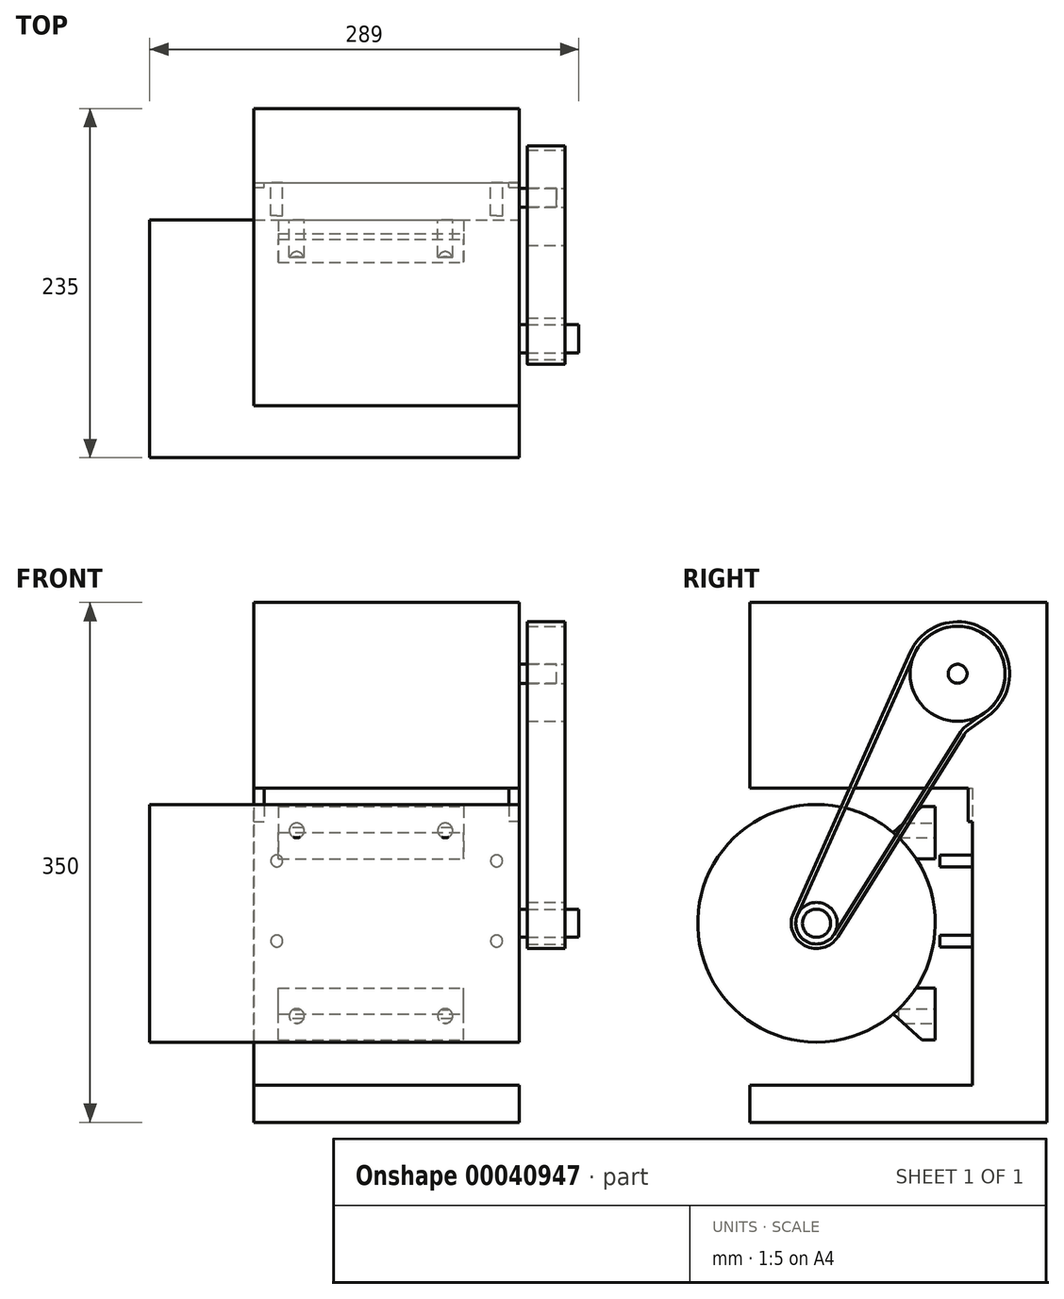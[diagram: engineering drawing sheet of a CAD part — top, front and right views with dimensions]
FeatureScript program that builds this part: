
annotation { "Feature Type Name" : "Feature", "Feature Type Description" : "" }
export const myFeature = defineFeature(function(context is Context, id is Id, definition is map)
    precondition{}
    {
        {
            var Q0;
            Q0=qCreatedBy(makeId("Right.planeOp"),FACE);
            var sketch = newSketch(context, id + "F0", { "sketchPlane" : qUnion([Q0])});
            skCircle(sketch, "E0", {"center": v(-10, 126) * mm, "radius": 6.38 * mm});
            skSolve(sketch);
        }
        {
            var Q0;
            Q0=makeQuery(id+"F0.imprint","IMPRINT",FACE,{"disambiguationData":[TD([[makeQuery(id+"F0.imprint","IMPRINT",EDGE,{"derivedFrom":sQuery(id+"F0.wireOp",EDGE,"E0")}),1.0]])]});
            extrude(context, id + "F1", {"entities" : qUnion([Q0]), "depth" : 25 * mm});
        }
        {
            var Q0;
            Q0=qCreatedBy(makeId("Right.planeOp"),FACE);
            var sketch = newSketch(context, id + "F2", { "sketchPlane" : qUnion([Q0])});
            skLineSegment(sketch, "E1", {"start": v(0, -151) * mm, "end": v(0, 49) * mm});
            skLineSegment(sketch, "E2", {"start": v(0, 49) * mm, "end": v(-150, 49) * mm});
            skLineSegment(sketch, "E3", {"start": v(-150, 49) * mm, "end": v(-150, 174) * mm});
            skLineSegment(sketch, "E4", {"start": v(-150, 174) * mm, "end": v(50, 174) * mm});
            skLineSegment(sketch, "E5", {"start": v(50, 174) * mm, "end": v(50, -176) * mm});
            skLineSegment(sketch, "E6", {"start": v(50, -176) * mm, "end": v(-150, -176) * mm});
            skLineSegment(sketch, "E7", {"start": v(-150, -176) * mm, "end": v(-150, -151) * mm});
            skLineSegment(sketch, "E8", {"start": v(-150, -151) * mm, "end": v(0, -151) * mm});
            skSolve(sketch);
        }
        {
            var Q0;
            Q0=makeQuery(id+"F2.imprint","IMPRINT",FACE,{"disambiguationData":[TD([[makeQuery(id+"F2.imprint","IMPRINT",EDGE,{"derivedFrom":sQuery(id+"F2.wireOp",EDGE,"E1")}),-1.0]])]});
            extrude(context, id + "F3", {"entities" : qUnion([Q0]), "operationType" : NewBodyOperationType.ADD, "oppositeDirection" : true, "depth" : (148 + 15.4 + 15.4) * mm});
        }
        {
            var Q0;
            Q0=qCreatedBy(makeId("Front.planeOp"),FACE);
            var sketch = newSketch(context, id + "F4", { "sketchPlane" : qUnion([Q0])});
            skCircle(sketch, "E9", {"center": v(-15.4, 0) * mm, "radius": 4 * mm});
            skCircle(sketch, "E10.0.1.0", {"center": v(-15.4, -54) * mm, "radius": 4 * mm});
            skCircle(sketch, "E10.1.0.0", {"center": v(-163.4, 0) * mm, "radius": 4 * mm});
            skCircle(sketch, "E10.1.1.0", {"center": v(-163.4, -54) * mm, "radius": 4 * mm});
            skLineSegment(sketch, "E10.direction1", {"start": v(-15.4, 0) * mm, "end": v(-163.4, 0) * mm, "construction": true});
            skLineSegment(sketch, "E10.direction2", {"start": v(-15.4, 0) * mm, "end": v(-15.4, -54) * mm, "construction": true});
            skSolve(sketch);
        }
        {
            var Q0;
            Q0=makeQuery(id+"F4.imprint","IMPRINT",FACE,{"disambiguationData":[TD([[makeQuery(id+"F4.imprint","IMPRINT",EDGE,{"derivedFrom":sQuery(id+"F4.wireOp",EDGE,"E9")}),1.0]])]});
            var Q1;
            Q1=makeQuery(id+"F4.imprint","IMPRINT",FACE,{"disambiguationData":[TD([[makeQuery(id+"F4.imprint","IMPRINT",EDGE,{"derivedFrom":sQuery(id+"F4.wireOp",EDGE,"E10.1.0.0")}),1.0]])]});
            var Q2;
            Q2=makeQuery(id+"F4.imprint","IMPRINT",FACE,{"disambiguationData":[TD([[makeQuery(id+"F4.imprint","IMPRINT",EDGE,{"derivedFrom":sQuery(id+"F4.wireOp",EDGE,"E10.1.1.0")}),1.0]])]});
            var Q3;
            Q3=makeQuery(id+"F4.imprint","IMPRINT",FACE,{"disambiguationData":[TD([[makeQuery(id+"F4.imprint","IMPRINT",EDGE,{"derivedFrom":sQuery(id+"F4.wireOp",EDGE,"E10.0.1.0")}),1.0]])]});
            extrude(context, id + "F5", {"entities" : qUnion([Q0, Q1, Q2, Q3]), "operationType" : NewBodyOperationType.ADD, "depth" : 22 * mm});
        }
        {
            var Q0;
            Q0=makeQuery(id+"F3.opExtrude","SWEPT_FACE",FACE,{"disambiguationData":[OSD([sQuery(id+"F2.wireOp",EDGE,"E1")])]});
            var sketch = newSketch(context, id + "F6", { "sketchPlane" : qUnion([Q0])});
            skLineSegment(sketch, "E11.bottom", {"start": v(0, 49) * mm, "end": v(-7, 49) * mm});
            skLineSegment(sketch, "E11.top", {"start": v(0, 26.4) * mm, "end": v(-7, 26.4) * mm});
            skLineSegment(sketch, "E11.left", {"start": v(0, 49) * mm, "end": v(0, 26.4) * mm});
            skLineSegment(sketch, "E11.right", {"start": v(-7, 49) * mm, "end": v(-7, 26.4) * mm});
            skLineSegment(sketch, "E12.bottom", {"start": v(-178.8, 49) * mm, "end": v(-171.8, 49) * mm});
            skLineSegment(sketch, "E12.top", {"start": v(-178.8, 26.4) * mm, "end": v(-171.8, 26.4) * mm});
            skLineSegment(sketch, "E12.left", {"start": v(-178.8, 49) * mm, "end": v(-178.8, 26.4) * mm});
            skLineSegment(sketch, "E12.right", {"start": v(-171.8, 49) * mm, "end": v(-171.8, 26.4) * mm});
            skSolve(sketch);
        }
        {
            var Q0;
            Q0=makeQuery(id+"F6.imprint","IMPRINT",FACE,{"disambiguationData":[TD([[makeQuery(id+"F6.imprint","IMPRINT",EDGE,{"derivedFrom":sQuery(id+"F6.wireOp",EDGE,"E11.bottom")}),-1.0]])]});
            var Q1;
            Q1=makeQuery(id+"F6.imprint","IMPRINT",FACE,{"disambiguationData":[TD([[makeQuery(id+"F6.imprint","IMPRINT",EDGE,{"derivedFrom":sQuery(id+"F6.wireOp",EDGE,"E12.bottom")}),-1.0]])]});
            extrude(context, id + "F7", {"entities" : qUnion([Q0, Q1]), "operationType" : NewBodyOperationType.ADD, "depth" : 3 * mm});
        }
        {
            var Q0;
            Q0=qCreatedBy(makeId("Right.planeOp"),FACE);
            var sketch = newSketch(context, id + "F8", { "sketchPlane" : qUnion([Q0])});
            skCircle(sketch, "E13", {"center": v(-105, -42) * mm, "radius": 80 * mm});
            skSolve(sketch);
        }
        {
            var Q0;
            Q0=makeQuery(id+"F8.imprint","IMPRINT",FACE,{"disambiguationData":[TD([[makeQuery(id+"F8.imprint","IMPRINT",EDGE,{"derivedFrom":sQuery(id+"F8.wireOp",EDGE,"E13")}),1.0]])]});
            extrude(context, id + "F9", {"entities" : qUnion([Q0]), "oppositeDirection" : true, "depth" : 249 * mm});
        }
        {
            var Q0;
            Q0=qCreatedBy(makeId("Right.planeOp"),FACE);
            cPlane(context, id + "F10", {"entities" : qUnion([Q0]), "cplaneType" : CPlaneType.OFFSET, "offset" : 37.5 * mm, "oppositeDirection" : true, "width" : 150 * mm, "height" : 150 * mm});
        }
        {
            var Q0;
            Q0=qCreatedBy(id+"F10.planeOp",FACE);
            var sketch = newSketch(context, id + "F11", { "sketchPlane" : qUnion([Q0])});
            skLineSegment(sketch, "E14", {"start": v(-25, 36.5) * mm, "end": v(-25, 1.5) * mm});
            skLineSegment(sketch, "E15", {"start": v(-25, 1.5) * mm, "end": v(-37.86, 1.5) * mm});
            skLineSegment(sketch, "E16", {"start": v(-25, 36.5) * mm, "end": v(-34, 36.5) * mm});
            skLineSegment(sketch, "E17", {"start": v(-34, 36.5) * mm, "end": v(-53.41, 19.15) * mm});
            skArc(sketch, "E18", {"start": v(-37.86, 1.5) * mm, "mid": v(-44.99, 10.9) * mm, "end": v(-53.41, 19.15) * mm});
            skLineSegment(sketch, "E19", {"start": v(-105, -42) * mm, "end": v(-57.73, -42) * mm});
            skLineSegment(sketch, "E20.MirrorCS", {"start": v(-25, -85.5) * mm, "end": v(-37.86, -85.5) * mm});
            skLineSegment(sketch, "E21.MirrorCS", {"start": v(-25, -120.5) * mm, "end": v(-25, -85.5) * mm});
            skLineSegment(sketch, "E22.MirrorCS", {"start": v(-34, -120.5) * mm, "end": v(-53.41, -103.15) * mm});
            skLineSegment(sketch, "E23.MirrorCS", {"start": v(-25, -120.5) * mm, "end": v(-34, -120.5) * mm});
            skArc(sketch, "E24.MirrorCS", {"start": v(-37.86, -85.5) * mm, "mid": v(-44.99, -94.9) * mm, "end": v(-53.41, -103.15) * mm});
            skSolve(sketch);
        }
        {
            var Q0;
            Q0=makeQuery(id+"F11.imprint","IMPRINT",FACE,{"disambiguationData":[TD([[makeQuery(id+"F11.imprint","IMPRINT",EDGE,{"derivedFrom":sQuery(id+"F11.wireOp",EDGE,"E14")}),-1.0]])]});
            var Q1;
            Q1=makeQuery(id+"F11.imprint","IMPRINT",FACE,{"disambiguationData":[TD([[makeQuery(id+"F11.imprint","IMPRINT",EDGE,{"derivedFrom":sQuery(id+"F11.wireOp",EDGE,"E20.MirrorCS")}),1.0]])]});
            extrude(context, id + "F12", {"entities" : qUnion([Q0, Q1]), "oppositeDirection" : true, "depth" : 125 * mm});
        }
        {
            var Q0;
            Q0=qCreatedBy(makeId("Right.planeOp"),FACE);
            cPlane(context, id + "F13", {"entities" : qUnion([Q0]), "cplaneType" : CPlaneType.OFFSET, "offset" : (46 - 15.4) * mm, "width" : 150 * mm, "height" : 150 * mm});
        }
        {
            var Q0;
            Q0=qCreatedBy(id+"F13.planeOp",FACE);
            var sketch = newSketch(context, id + "F14", { "sketchPlane" : qUnion([Q0])});
            skCircle(sketch, "E25", {"center": v(-10, 126) * mm, "radius": 32 * mm});
            skCircle(sketch, "E26", {"center": v(-10, 126) * mm, "radius": 6.38 * mm});
            skSolve(sketch);
        }
        {
            var Q0;
            Q0=makeQuery(id+"F14.imprint","IMPRINT",FACE,{"disambiguationData":[TD([[makeQuery(id+"F14.imprint","IMPRINT",EDGE,{"derivedFrom":sQuery(id+"F14.wireOp",EDGE,"E25")}),1.0]])]});
            extrude(context, id + "F15", {"entities" : qUnion([Q0]), "oppositeDirection" : true, "depth" : 25.4 * mm});
        }
        {
            var Q0;
            Q0=qCreatedBy(id+"F13.planeOp",FACE);
            var sketch = newSketch(context, id + "F16", { "sketchPlane" : qUnion([Q0])});
            skCircle(sketch, "E27", {"center": v(-105, -42) * mm, "radius": 14 * mm});
            skCircle(sketch, "E28", {"center": v(-105, -42) * mm, "radius": 9.5 * mm});
            skSolve(sketch);
        }
        {
            var Q0;
            Q0=makeQuery(id+"F16.imprint","IMPRINT",FACE,{"disambiguationData":[TD([[makeQuery(id+"F16.imprint","IMPRINT",EDGE,{"derivedFrom":sQuery(id+"F16.wireOp",EDGE,"E27")}),1.0]])]});
            extrude(context, id + "F17", {"entities" : qUnion([Q0]), "oppositeDirection" : true, "depth" : 25.4 * mm});
        }
        {
            var Q0;
            Q0=makeQuery(id+"F12.opExtrude","SWEPT_FACE",FACE,{"disambiguationData":[OSD([sQuery(id+"F11.wireOp",EDGE,"E21.MirrorCS")])]});
            var sketch = newSketch(context, id + "F18", { "sketchPlane" : qUnion([Q0])});
            skCircle(sketch, "E29", {"center": v(50, 20.5) * mm, "radius": 5 * mm});
            skCircle(sketch, "E30.0.1.0", {"center": v(50, -104.5) * mm, "radius": 5 * mm});
            skCircle(sketch, "E30.1.0.0", {"center": v(150, 20.5) * mm, "radius": 5 * mm});
            skCircle(sketch, "E30.1.1.0", {"center": v(150, -104.5) * mm, "radius": 5 * mm});
            skLineSegment(sketch, "E30.direction1", {"start": v(50, 20.5) * mm, "end": v(150, 20.5) * mm, "construction": true});
            skLineSegment(sketch, "E30.direction2", {"start": v(50, 20.5) * mm, "end": v(50, -104.5) * mm, "construction": true});
            skSolve(sketch);
        }
        {
            var Q0;
            Q0=makeQuery(id+"F18.imprint","IMPRINT",FACE,{"disambiguationData":[TD([[makeQuery(id+"F18.imprint","IMPRINT",EDGE,{"derivedFrom":sQuery(id+"F18.wireOp",EDGE,"E29")}),1.0]])]});
            var Q1;
            Q1=makeQuery(id+"F18.imprint","IMPRINT",FACE,{"disambiguationData":[TD([[makeQuery(id+"F18.imprint","IMPRINT",EDGE,{"derivedFrom":sQuery(id+"F18.wireOp",EDGE,"E30.1.0.0")}),1.0]])]});
            var Q2;
            Q2=makeQuery(id+"F18.imprint","IMPRINT",FACE,{"disambiguationData":[TD([[makeQuery(id+"F18.imprint","IMPRINT",EDGE,{"derivedFrom":sQuery(id+"F18.wireOp",EDGE,"E30.1.1.0")}),1.0]])]});
            var Q3;
            Q3=makeQuery(id+"F18.imprint","IMPRINT",FACE,{"disambiguationData":[TD([[makeQuery(id+"F18.imprint","IMPRINT",EDGE,{"derivedFrom":sQuery(id+"F18.wireOp",EDGE,"E30.0.1.0")}),1.0]])]});
            extrude(context, id + "F19", {"entities" : qUnion([Q0, Q1, Q2, Q3]), "operationType" : NewBodyOperationType.REMOVE, "oppositeDirection" : true, "depth" : 25 * mm});
        }
        {
            var Q0;
            Q0=makeQuery(id+"F9.opExtrude","CAP_FACE",FACE,{"disambiguationData":[OSD([sQuery(id+"F8.wireOp",EDGE,"E13")])],"isStart":true});
            var sketch = newSketch(context, id + "F20", { "sketchPlane" : qUnion([Q0])});
            skCircle(sketch, "E31", {"center": v(-105, -42) * mm, "radius": 9.5 * mm});
            skSolve(sketch);
        }
        {
            var Q0;
            Q0=makeQuery(id+"F20.imprint","IMPRINT",FACE,{"disambiguationData":[TD([[makeQuery(id+"F20.imprint","IMPRINT",EDGE,{"derivedFrom":sQuery(id+"F20.wireOp",EDGE,"E31")}),1.0]])]});
            extrude(context, id + "F21", {"entities" : qUnion([Q0]), "depth" : 40 * mm});
        }
        {
            var Q0;
            Q0=qCreatedBy(id+"F13.planeOp",FACE);
            var sketch = newSketch(context, id + "F22", { "sketchPlane" : qUnion([Q0])});
            skArc(sketch, "E32.0", {"start": v(8.64, 100) * mm, "mid": v(10.25, 150.78) * mm, "end": v(-39.2, 139.08) * mm});
            skArc(sketch, "E33.0", {"start": v(-117.78, -36.28) * mm, "mid": v(-111.59, -54.35) * mm, "end": v(-93.13, -49.42) * mm});
            skLineSegment(sketch, "E34", {"start": v(-117.78, -36.28) * mm, "end": v(-39.2, 139.08) * mm});
            skLineSegment(sketch, "E35", {"start": v(8.64, 100) * mm, "end": v(-4.5, 90.57) * mm});
            skLineSegment(sketch, "E36", {"start": v(-93.13, -49.42) * mm, "end": v(-7.96, 86.89) * mm});
            skArc(sketch, "E37", {"start": v(-4.5, 90.57) * mm, "mid": v(-6.41, 88.9) * mm, "end": v(-7.96, 86.89) * mm});
            skArc(sketch, "E38.0", {"start": v(-120.51, -35.05) * mm, "mid": v(-113, -57) * mm, "end": v(-90.58, -51) * mm});
            skArc(sketch, "E38.1", {"start": v(10.4, 97.55) * mm, "mid": v(12.15, 153.1) * mm, "end": v(-41.94, 140.31) * mm});
            skLineSegment(sketch, "E38.2", {"start": v(10.4, 97.55) * mm, "end": v(-2.76, 88.13) * mm});
            skLineSegment(sketch, "E38.3", {"start": v(-120.51, -35.05) * mm, "end": v(-41.94, 140.31) * mm});
            skArc(sketch, "E38.4", {"start": v(-2.76, 88.13) * mm, "mid": v(-4.22, 86.84) * mm, "end": v(-5.41, 85.3) * mm});
            skLineSegment(sketch, "E38.5", {"start": v(-90.58, -51) * mm, "end": v(-5.41, 85.3) * mm});
            skSolve(sketch);
        }
        {
            var Q0;
            Q0=makeQuery(id+"F22.imprint","IMPRINT",FACE,{"disambiguationData":[TD([[makeQuery(id+"F22.imprint","IMPRINT",EDGE,{"derivedFrom":sQuery(id+"F22.wireOp",EDGE,"E32.0")}),-1.0]])]});
            extrude(context, id + "F23", {"entities" : qUnion([Q0]), "oppositeDirection" : true, "depth" : 25.4 * mm});
        }
    });
